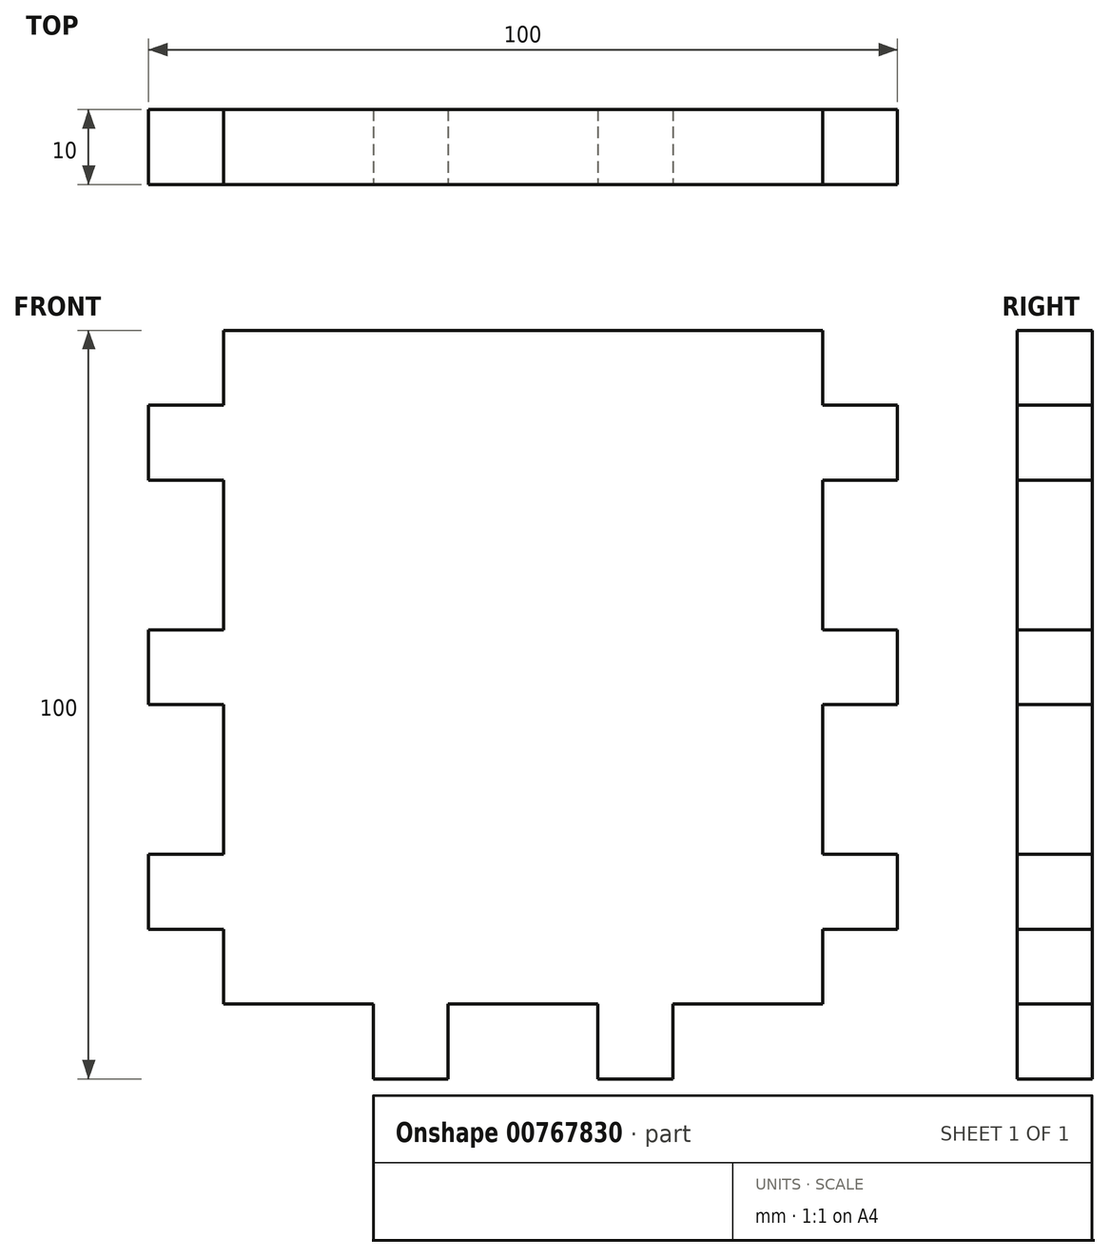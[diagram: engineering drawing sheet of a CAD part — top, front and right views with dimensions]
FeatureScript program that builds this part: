
annotation { "Feature Type Name" : "Feature", "Feature Type Description" : "" }
export const myFeature = defineFeature(function(context is Context, id is Id, definition is map)
    precondition{}
    {
        {
            var Q0;
            Q0=qCreatedBy(makeId("Front.planeOp"),FACE);
            var sketch = newSketch(context, id + "F0", { "sketchPlane" : qUnion([Q0])});
            skLineSegment(sketch, "E0.bottom", {"start": v(-46.73, 47.83) * mm, "end": v(53.27, 47.83) * mm});
            skLineSegment(sketch, "E0.top", {"start": v(-46.73, -52.17) * mm, "end": v(53.27, -52.17) * mm});
            skLineSegment(sketch, "E0.left", {"start": v(-46.73, 47.83) * mm, "end": v(-46.73, -52.17) * mm});
            skLineSegment(sketch, "E0.right", {"start": v(53.27, 47.83) * mm, "end": v(53.27, -52.17) * mm});
            skSolve(sketch);
        }
        {
            var Q0;
            Q0 = qSketchRegion(id + "F0", true);
            extrude(context, id + "F1", {"entities" : qUnion([Q0]), "depth" : 10 * mm, "offsetDistance" : 25 * mm});
        }
        {
            var Q0;
            Q0=makeQuery(id+"F1.opExtrude","CAP_FACE",FACE,{"disambiguationData":[OSD([sQuery(id+"F0.wireOp",EDGE,"E0.bottom"),sQuery(id+"F0.wireOp",EDGE,"E0.top"),sQuery(id+"F0.wireOp",EDGE,"E0.left"),sQuery(id+"F0.wireOp",EDGE,"E0.right")])],"isStart":false});
            var sketch = newSketch(context, id + "F2", { "sketchPlane" : qUnion([Q0])});
            skLineSegment(sketch, "E1.bottom", {"start": v(-46.73, 47.83) * mm, "end": v(-36.73, 47.83) * mm});
            skLineSegment(sketch, "E1.top", {"start": v(-46.73, 37.83) * mm, "end": v(-36.73, 37.83) * mm});
            skLineSegment(sketch, "E1.left", {"start": v(-46.73, 47.83) * mm, "end": v(-46.73, 37.83) * mm});
            skLineSegment(sketch, "E1.right", {"start": v(-36.73, 47.83) * mm, "end": v(-36.73, 37.83) * mm});
            skSolve(sketch);
        }
        {
            var Q0;
            Q0 = qSketchRegion(id + "F2", true);
            extrude(context, id + "F3", {"entities" : qUnion([Q0]), "operationType" : NewBodyOperationType.REMOVE, "oppositeDirection" : true, "depth" : 10 * mm, "offsetDistance" : 25 * mm});
        }
        {
            var Q0;
            Q0=makeQuery(id+"F1.opExtrude","CAP_FACE",FACE,{"disambiguationData":[OSD([sQuery(id+"F0.wireOp",EDGE,"E0.bottom"),sQuery(id+"F0.wireOp",EDGE,"E0.top"),sQuery(id+"F0.wireOp",EDGE,"E0.left"),sQuery(id+"F0.wireOp",EDGE,"E0.right")])],"isStart":false});
            var sketch = newSketch(context, id + "F4", { "sketchPlane" : qUnion([Q0])});
            skLineSegment(sketch, "E2.bottom", {"start": v(-46.73, 27.83) * mm, "end": v(-36.73, 27.83) * mm});
            skLineSegment(sketch, "E2.top", {"start": v(-46.73, 7.83) * mm, "end": v(-36.73, 7.83) * mm});
            skLineSegment(sketch, "E2.left", {"start": v(-46.73, 27.83) * mm, "end": v(-46.73, 7.83) * mm});
            skLineSegment(sketch, "E2.right", {"start": v(-36.73, 27.83) * mm, "end": v(-36.73, 7.83) * mm});
            skSolve(sketch);
        }
        {
            var Q0;
            Q0 = qSketchRegion(id + "F4", true);
            extrude(context, id + "F5", {"entities" : qUnion([Q0]), "operationType" : NewBodyOperationType.REMOVE, "oppositeDirection" : true, "depth" : 10 * mm, "offsetDistance" : 25 * mm});
        }
        {
            var Q0;
            Q0=makeQuery(id+"F1.opExtrude","CAP_FACE",FACE,{"disambiguationData":[OSD([sQuery(id+"F0.wireOp",EDGE,"E0.bottom"),sQuery(id+"F0.wireOp",EDGE,"E0.top"),sQuery(id+"F0.wireOp",EDGE,"E0.left"),sQuery(id+"F0.wireOp",EDGE,"E0.right")])],"isStart":false});
            var sketch = newSketch(context, id + "F6", { "sketchPlane" : qUnion([Q0])});
            skLineSegment(sketch, "E3.bottom", {"start": v(-46.73, -2.17) * mm, "end": v(-36.73, -2.17) * mm});
            skLineSegment(sketch, "E3.top", {"start": v(-46.73, -22.17) * mm, "end": v(-36.73, -22.17) * mm});
            skLineSegment(sketch, "E3.left", {"start": v(-46.73, -2.17) * mm, "end": v(-46.73, -22.17) * mm});
            skLineSegment(sketch, "E3.right", {"start": v(-36.73, -2.17) * mm, "end": v(-36.73, -22.17) * mm});
            skSolve(sketch);
        }
        {
            var Q0;
            Q0 = qSketchRegion(id + "F6", true);
            extrude(context, id + "F7", {"entities" : qUnion([Q0]), "operationType" : NewBodyOperationType.REMOVE, "oppositeDirection" : true, "depth" : 10 * mm, "offsetDistance" : 25 * mm});
        }
        {
            var Q0;
            Q0=makeQuery(id+"F1.opExtrude","CAP_FACE",FACE,{"disambiguationData":[OSD([sQuery(id+"F0.wireOp",EDGE,"E0.bottom"),sQuery(id+"F0.wireOp",EDGE,"E0.top"),sQuery(id+"F0.wireOp",EDGE,"E0.left"),sQuery(id+"F0.wireOp",EDGE,"E0.right")])],"isStart":false});
            var sketch = newSketch(context, id + "F8", { "sketchPlane" : qUnion([Q0])});
            skLineSegment(sketch, "E4.bottom", {"start": v(-46.73, -32.17) * mm, "end": v(-36.73, -32.17) * mm});
            skLineSegment(sketch, "E4.top", {"start": v(-46.73, -52.17) * mm, "end": v(-36.73, -52.17) * mm});
            skLineSegment(sketch, "E4.left", {"start": v(-46.73, -32.17) * mm, "end": v(-46.73, -52.17) * mm});
            skLineSegment(sketch, "E4.right", {"start": v(-36.73, -32.17) * mm, "end": v(-36.73, -52.17) * mm});
            skSolve(sketch);
        }
        {
            var Q0;
            Q0 = qSketchRegion(id + "F8", true);
            extrude(context, id + "F9", {"entities" : qUnion([Q0]), "operationType" : NewBodyOperationType.REMOVE, "oppositeDirection" : true, "depth" : 10 * mm, "offsetDistance" : 25 * mm});
        }
        {
            var Q0;
            Q0=makeQuery(id+"F1.opExtrude","CAP_FACE",FACE,{"disambiguationData":[OSD([sQuery(id+"F0.wireOp",EDGE,"E0.bottom"),sQuery(id+"F0.wireOp",EDGE,"E0.top"),sQuery(id+"F0.wireOp",EDGE,"E0.left"),sQuery(id+"F0.wireOp",EDGE,"E0.right")])],"isStart":false});
            var sketch = newSketch(context, id + "F10", { "sketchPlane" : qUnion([Q0])});
            skLineSegment(sketch, "E5.bottom", {"start": v(-36.73, -42.17) * mm, "end": v(-16.73, -42.17) * mm});
            skLineSegment(sketch, "E5.top", {"start": v(-36.73, -52.17) * mm, "end": v(-16.73, -52.17) * mm});
            skLineSegment(sketch, "E5.left", {"start": v(-36.73, -42.17) * mm, "end": v(-36.73, -52.17) * mm});
            skLineSegment(sketch, "E5.right", {"start": v(-16.73, -42.17) * mm, "end": v(-16.73, -52.17) * mm});
            skSolve(sketch);
        }
        {
            var Q0;
            Q0 = qSketchRegion(id + "F10", true);
            extrude(context, id + "F11", {"entities" : qUnion([Q0]), "operationType" : NewBodyOperationType.REMOVE, "oppositeDirection" : true, "depth" : 10 * mm, "offsetDistance" : 25 * mm});
        }
        {
            var Q0;
            Q0=makeQuery(id+"F1.opExtrude","CAP_FACE",FACE,{"disambiguationData":[OSD([sQuery(id+"F0.wireOp",EDGE,"E0.bottom"),sQuery(id+"F0.wireOp",EDGE,"E0.top"),sQuery(id+"F0.wireOp",EDGE,"E0.left"),sQuery(id+"F0.wireOp",EDGE,"E0.right")])],"isStart":false});
            var sketch = newSketch(context, id + "F12", { "sketchPlane" : qUnion([Q0])});
            skLineSegment(sketch, "E6.bottom", {"start": v(-6.73, -52.17) * mm, "end": v(13.27, -52.17) * mm});
            skLineSegment(sketch, "E6.top", {"start": v(-6.73, -42.17) * mm, "end": v(13.27, -42.17) * mm});
            skLineSegment(sketch, "E6.left", {"start": v(-6.73, -52.17) * mm, "end": v(-6.73, -42.17) * mm});
            skLineSegment(sketch, "E6.right", {"start": v(13.27, -52.17) * mm, "end": v(13.27, -42.17) * mm});
            skSolve(sketch);
        }
        {
            var Q0;
            Q0 = qSketchRegion(id + "F12", true);
            extrude(context, id + "F13", {"entities" : qUnion([Q0]), "operationType" : NewBodyOperationType.REMOVE, "oppositeDirection" : true, "depth" : 10 * mm, "offsetDistance" : 25 * mm});
        }
        {
            var Q0;
            Q0=makeQuery(id+"F1.opExtrude","CAP_FACE",FACE,{"disambiguationData":[OSD([sQuery(id+"F0.wireOp",EDGE,"E0.bottom"),sQuery(id+"F0.wireOp",EDGE,"E0.top"),sQuery(id+"F0.wireOp",EDGE,"E0.left"),sQuery(id+"F0.wireOp",EDGE,"E0.right")])],"isStart":false});
            var sketch = newSketch(context, id + "F14", { "sketchPlane" : qUnion([Q0])});
            skLineSegment(sketch, "E7.bottom", {"start": v(23.27, -52.17) * mm, "end": v(43.27, -52.17) * mm});
            skLineSegment(sketch, "E7.top", {"start": v(23.27, -42.17) * mm, "end": v(43.27, -42.17) * mm});
            skLineSegment(sketch, "E7.left", {"start": v(23.27, -52.17) * mm, "end": v(23.27, -42.17) * mm});
            skLineSegment(sketch, "E7.right", {"start": v(43.27, -52.17) * mm, "end": v(43.27, -42.17) * mm});
            skSolve(sketch);
        }
        {
            var Q0;
            Q0 = qSketchRegion(id + "F14", true);
            extrude(context, id + "F15", {"entities" : qUnion([Q0]), "operationType" : NewBodyOperationType.REMOVE, "oppositeDirection" : true, "depth" : 10 * mm, "offsetDistance" : 25 * mm});
        }
        {
            var Q0;
            Q0=makeQuery(id+"F1.opExtrude","CAP_FACE",FACE,{"disambiguationData":[OSD([sQuery(id+"F0.wireOp",EDGE,"E0.bottom"),sQuery(id+"F0.wireOp",EDGE,"E0.top"),sQuery(id+"F0.wireOp",EDGE,"E0.left"),sQuery(id+"F0.wireOp",EDGE,"E0.right")])],"isStart":false});
            var sketch = newSketch(context, id + "F16", { "sketchPlane" : qUnion([Q0])});
            skLineSegment(sketch, "E8.bottom", {"start": v(53.27, 47.83) * mm, "end": v(43.27, 47.83) * mm});
            skLineSegment(sketch, "E8.top", {"start": v(53.27, 37.83) * mm, "end": v(43.27, 37.83) * mm});
            skLineSegment(sketch, "E8.left", {"start": v(53.27, 47.83) * mm, "end": v(53.27, 37.83) * mm});
            skLineSegment(sketch, "E8.right", {"start": v(43.27, 47.83) * mm, "end": v(43.27, 37.83) * mm});
            skSolve(sketch);
        }
        {
            var Q0;
            Q0 = qSketchRegion(id + "F16", true);
            extrude(context, id + "F17", {"entities" : qUnion([Q0]), "operationType" : NewBodyOperationType.REMOVE, "oppositeDirection" : true, "depth" : 10 * mm, "offsetDistance" : 25 * mm});
        }
        {
            var Q0;
            Q0=makeQuery(id+"F1.opExtrude","CAP_FACE",FACE,{"disambiguationData":[OSD([sQuery(id+"F0.wireOp",EDGE,"E0.bottom"),sQuery(id+"F0.wireOp",EDGE,"E0.top"),sQuery(id+"F0.wireOp",EDGE,"E0.left"),sQuery(id+"F0.wireOp",EDGE,"E0.right")])],"isStart":false});
            var sketch = newSketch(context, id + "F18", { "sketchPlane" : qUnion([Q0])});
            skLineSegment(sketch, "E9.bottom", {"start": v(53.27, 27.83) * mm, "end": v(43.27, 27.83) * mm});
            skLineSegment(sketch, "E9.top", {"start": v(53.27, 7.83) * mm, "end": v(43.27, 7.83) * mm});
            skLineSegment(sketch, "E9.left", {"start": v(53.27, 27.83) * mm, "end": v(53.27, 7.83) * mm});
            skLineSegment(sketch, "E9.right", {"start": v(43.27, 27.83) * mm, "end": v(43.27, 7.83) * mm});
            skSolve(sketch);
        }
        {
            var Q0;
            Q0 = qSketchRegion(id + "F18", true);
            extrude(context, id + "F19", {"entities" : qUnion([Q0]), "operationType" : NewBodyOperationType.REMOVE, "oppositeDirection" : true, "depth" : 10 * mm, "offsetDistance" : 25 * mm});
        }
        {
            var Q0;
            Q0=makeQuery(id+"F1.opExtrude","CAP_FACE",FACE,{"disambiguationData":[OSD([sQuery(id+"F0.wireOp",EDGE,"E0.bottom"),sQuery(id+"F0.wireOp",EDGE,"E0.top"),sQuery(id+"F0.wireOp",EDGE,"E0.left"),sQuery(id+"F0.wireOp",EDGE,"E0.right")])],"isStart":false});
            var sketch = newSketch(context, id + "F20", { "sketchPlane" : qUnion([Q0])});
            skLineSegment(sketch, "E10.bottom", {"start": v(53.27, -2.17) * mm, "end": v(43.27, -2.17) * mm});
            skLineSegment(sketch, "E10.top", {"start": v(53.27, -22.17) * mm, "end": v(43.27, -22.17) * mm});
            skLineSegment(sketch, "E10.left", {"start": v(53.27, -2.17) * mm, "end": v(53.27, -22.17) * mm});
            skLineSegment(sketch, "E10.right", {"start": v(43.27, -2.17) * mm, "end": v(43.27, -22.17) * mm});
            skSolve(sketch);
        }
        {
            var Q0;
            Q0 = qSketchRegion(id + "F20", true);
            extrude(context, id + "F21", {"entities" : qUnion([Q0]), "operationType" : NewBodyOperationType.REMOVE, "oppositeDirection" : true, "depth" : 10 * mm, "offsetDistance" : 25 * mm});
        }
        {
            var Q0;
            Q0=makeQuery(id+"F1.opExtrude","CAP_FACE",FACE,{"disambiguationData":[OSD([sQuery(id+"F0.wireOp",EDGE,"E0.bottom"),sQuery(id+"F0.wireOp",EDGE,"E0.top"),sQuery(id+"F0.wireOp",EDGE,"E0.left"),sQuery(id+"F0.wireOp",EDGE,"E0.right")])],"isStart":false});
            var sketch = newSketch(context, id + "F22", { "sketchPlane" : qUnion([Q0])});
            skLineSegment(sketch, "E11.bottom", {"start": v(53.27, -52.17) * mm, "end": v(43.27, -52.17) * mm});
            skLineSegment(sketch, "E11.top", {"start": v(53.27, -32.17) * mm, "end": v(43.27, -32.17) * mm});
            skLineSegment(sketch, "E11.left", {"start": v(53.27, -52.17) * mm, "end": v(53.27, -32.17) * mm});
            skLineSegment(sketch, "E11.right", {"start": v(43.27, -52.17) * mm, "end": v(43.27, -32.17) * mm});
            skSolve(sketch);
        }
        {
            var Q0;
            Q0 = qSketchRegion(id + "F22", true);
            extrude(context, id + "F23", {"entities" : qUnion([Q0]), "operationType" : NewBodyOperationType.REMOVE, "oppositeDirection" : true, "depth" : 10 * mm, "offsetDistance" : 25 * mm});
        }
    });
